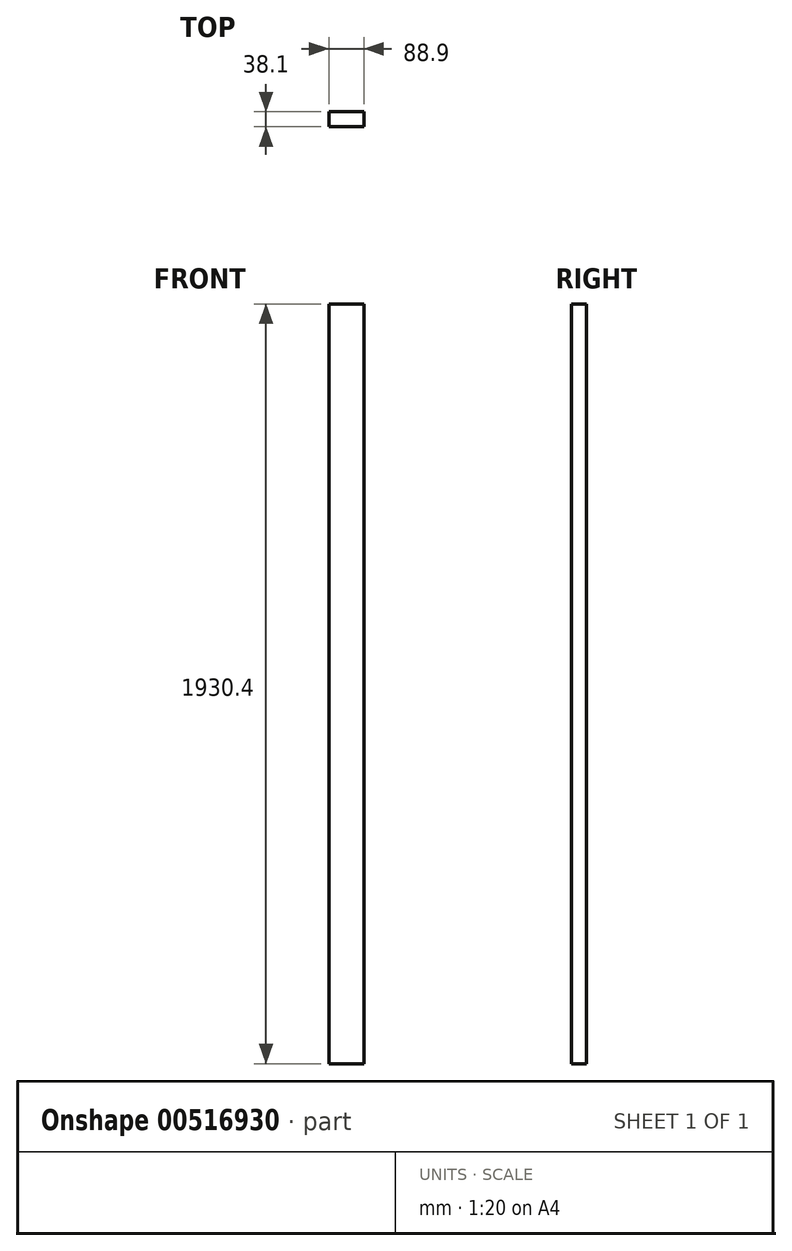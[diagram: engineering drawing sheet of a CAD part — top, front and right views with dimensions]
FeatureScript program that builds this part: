
annotation { "Feature Type Name" : "Feature", "Feature Type Description" : "" }
export const myFeature = defineFeature(function(context is Context, id is Id, definition is map)
    precondition{}
    {
        {
            var Q0;
            Q0=qCreatedBy(makeId("Front.planeOp"),FACE);
            var sketch = newSketch(context, id + "F0", { "sketchPlane" : qUnion([Q0])});
            skLineSegment(sketch, "E0.bottom", {"start": v(0, 0) * mm, "end": v(88.9, 0) * mm});
            skLineSegment(sketch, "E0.top", {"start": v(0, 1930.4) * mm, "end": v(88.9, 1930.4) * mm});
            skLineSegment(sketch, "E0.left", {"start": v(0, 0) * mm, "end": v(0, 1930.4) * mm});
            skLineSegment(sketch, "E0.right", {"start": v(88.9, 0) * mm, "end": v(88.9, 1930.4) * mm});
            skSolve(sketch);
        }
        {
            var Q0;
            Q0 = qSketchRegion(id + "F0", true);
            extrude(context, id + "F1", {"entities" : qUnion([Q0]), "depth" : 38.1 * mm, "offsetDistance" : 25.4 * mm});
        }
    });
